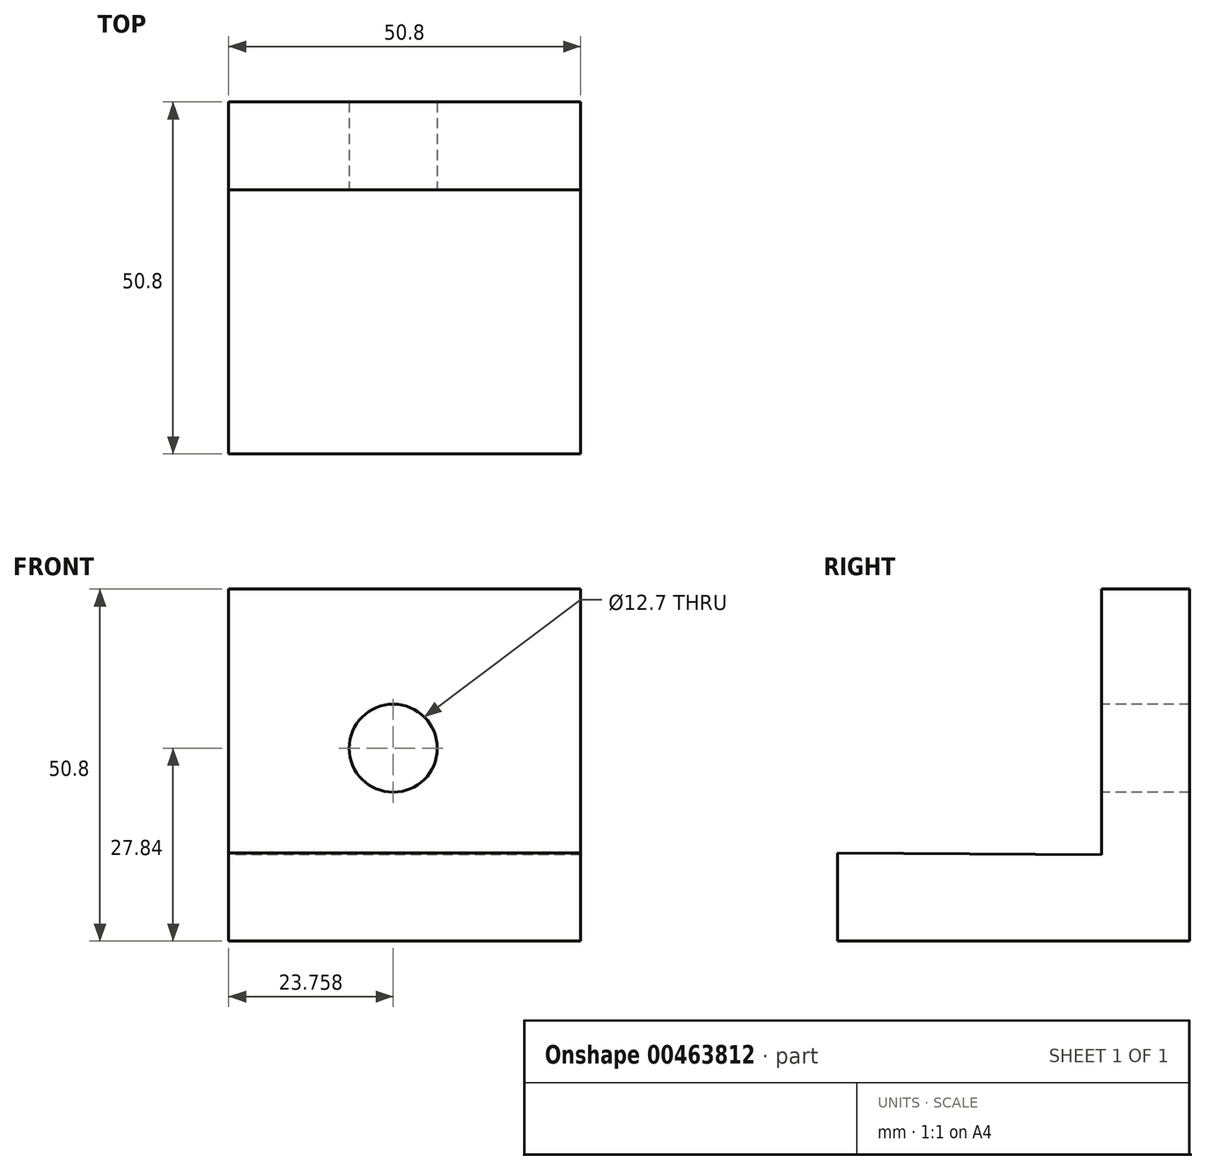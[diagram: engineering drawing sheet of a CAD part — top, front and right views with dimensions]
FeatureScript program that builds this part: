
annotation { "Feature Type Name" : "Feature", "Feature Type Description" : "" }
export const myFeature = defineFeature(function(context is Context, id is Id, definition is map)
    precondition{}
    {
        {
            var Q0;
            Q0=qCreatedBy(makeId("Right.planeOp"),FACE);
            var sketch = newSketch(context, id + "F0", { "sketchPlane" : qUnion([Q0])});
            skLineSegment(sketch, "E0", {"start": v(42.92, 22.96) * mm, "end": v(42.92, -27.84) * mm});
            skLineSegment(sketch, "E1", {"start": v(42.92, -27.84) * mm, "end": v(-7.88, -27.84) * mm});
            skLineSegment(sketch, "E2", {"start": v(-7.88, -27.84) * mm, "end": v(-7.88, -15.14) * mm});
            skLineSegment(sketch, "E3", {"start": v(42.92, 22.96) * mm, "end": v(30.22, 22.96) * mm});
            skLineSegment(sketch, "E4", {"start": v(30.22, 22.96) * mm, "end": v(30.22, -15.37) * mm});
            skLineSegment(sketch, "E5", {"start": v(30.22, -15.37) * mm, "end": v(-7.88, -15.14) * mm});
            skSolve(sketch);
        }
        {
            var Q0;
            Q0 = qSketchRegion(id + "F0", true);
            extrude(context, id + "F1", {"entities" : qUnion([Q0]), "depth" : 50.8 * mm});
        }
        {
            var Q0;
            Q0=makeQuery(id+"F1.opExtrude","SWEPT_FACE",FACE,{"disambiguationData":[OSD([sQuery(id+"F0.wireOp",EDGE,"E4")])]});
            var sketch = newSketch(context, id + "F2", { "sketchPlane" : qUnion([Q0])});
            skCircle(sketch, "E6", {"center": v(23.76, 0) * mm, "radius": 6.35 * mm});
            skSolve(sketch);
        }
        {
            var Q0;
            Q0 = qSketchRegion(id + "F2", true);
            extrude(context, id + "F3", {"entities" : qUnion([Q0]), "operationType" : NewBodyOperationType.REMOVE, "oppositeDirection" : true, "depth" : 25.4 * mm});
        }
    });
